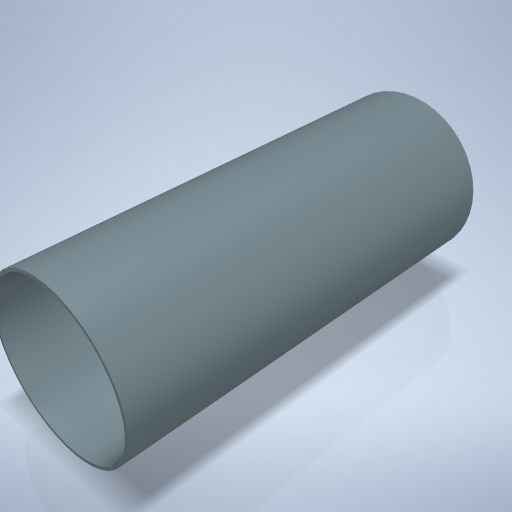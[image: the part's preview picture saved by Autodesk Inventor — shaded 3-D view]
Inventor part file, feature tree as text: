
AUTODESK INVENTOR PART (.ipt)
format: ipt  version: 2024.2 (Build 282272000, 272)  size: 233,472 bytes
history: native  units: mm
features: extrude x1, sketch x1
ambient origin geometry x8: Origin, YZ Plane, XZ Plane, XY Plane, X Axis, Y Axis, Z Axis, Center Point
bodies: Volumenkörper1 (feature_tree)
feature tree (2):
  extrude  "Extrusion1"  Depth=63.0mm
  sketch  "Skizze1"  dims[d0=25.5mm d1=24.5mm d2=63.0mm d3=0.0mm]
